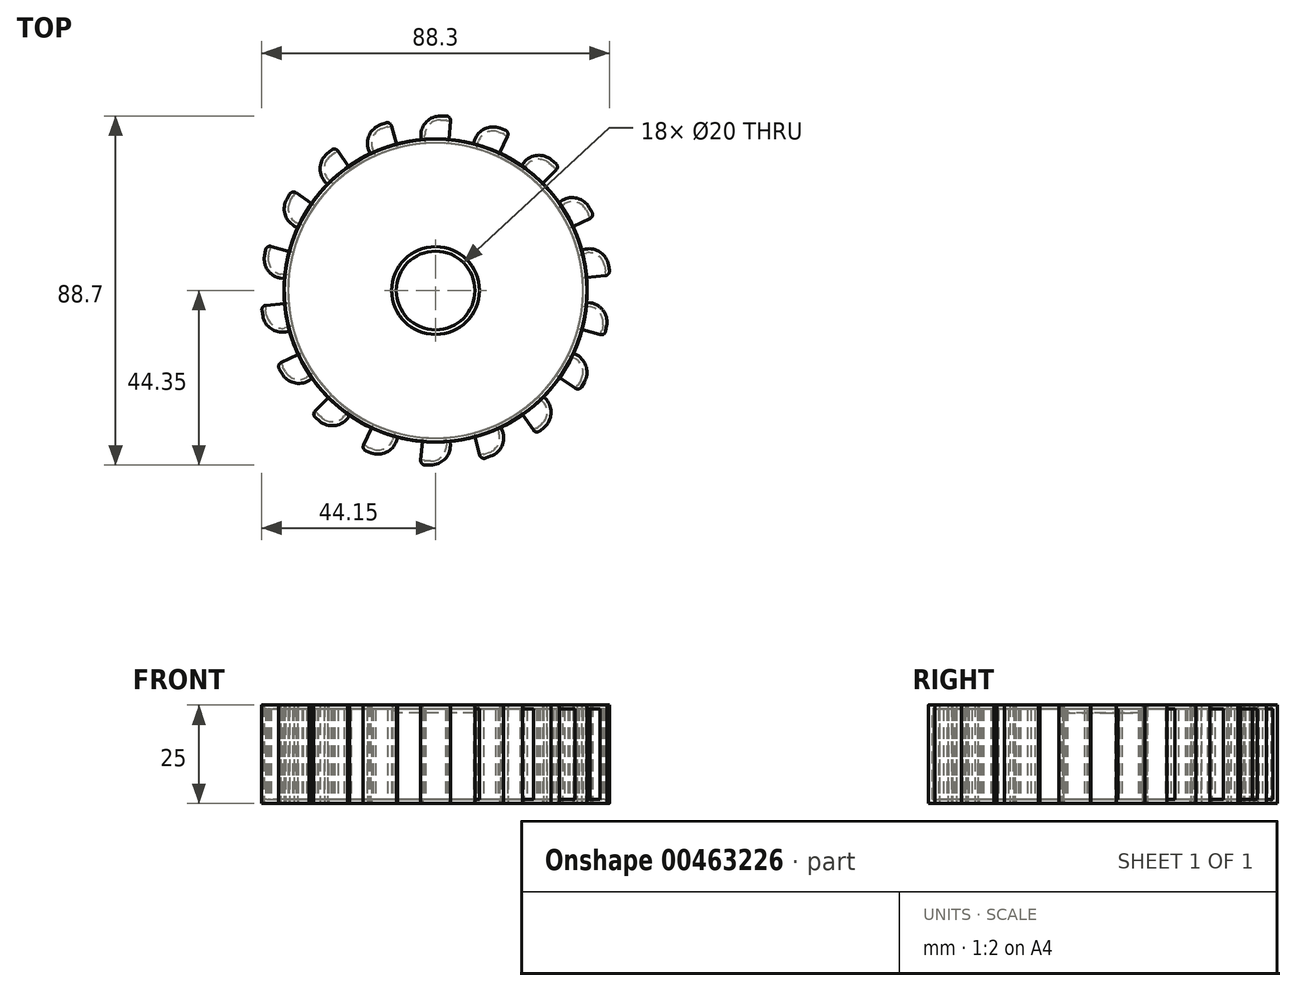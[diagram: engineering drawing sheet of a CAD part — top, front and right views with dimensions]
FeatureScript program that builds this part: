
annotation { "Feature Type Name" : "Feature", "Feature Type Description" : "" }
export const myFeature = defineFeature(function(context is Context, id is Id, definition is map)
    precondition{}
    {
        {
            var Q0;
            Q0=qCreatedBy(makeId("Top.planeOp"),FACE);
            var sketch = newSketch(context, id + "F0", { "sketchPlane" : qUnion([Q0])});
            skCircle(sketch, "E0", {"center": v(0, 0) * mm, "radius": 38.5 * mm});
            skLineSegment(sketch, "E1", {"start": v(1.24, 44.35) * mm, "end": v(2.65, 44.35) * mm});
            skArc(sketch, "E2.filletArc", {"start": v(1.24, 44.35) * mm, "mid": v(-2.3, 42.88) * mm, "end": v(-3.76, 39.35) * mm});
            skArc(sketch, "E3.filletArc", {"start": v(3.77, 43.12) * mm, "mid": v(3.48, 43.98) * mm, "end": v(2.65, 44.35) * mm});
            skLineSegment(sketch, "E4.trimOffspring", {"start": v(-3.67, 38.32) * mm, "end": v(-3.76, 39.35) * mm});
            skLineSegment(sketch, "E5.trimOffspring", {"start": v(3.35, 38.35) * mm, "end": v(3.77, 43.12) * mm});
            skPoint(sketch, "E6.orphan", {"position": v(0, 57.06) * mm});
            skCircle(sketch, "E7", {"center": v(0, 0) * mm, "radius": 10 * mm});
            skSolve(sketch);
        }
        {
            var Q0;
            {var subQ0=sQuery(id+"F0.wireOp",EDGE,"E0");var subQ1=makeQuery(id+"F0.imprint","INTERSECT",VERTEX,{"derivedFrom":[subQ0,sQuery(id+"F0.wireOp",EDGE,"E4.trimOffspring")]});Q0=makeQuery(id+"F0.imprint","IMPRINT",FACE,{"disambiguationData":[TD([[makeQuery(id+"F0.imprint","IMPRINT",EDGE,{"disambiguationData":[TD([[subQ1,1.0]])],"derivedFrom":subQ0}),1.0]])]});}
            var Q1;
            Q1=makeQuery(id+"F0.imprint","IMPRINT",FACE,{"disambiguationData":[TD([[makeQuery(id+"F0.imprint","IMPRINT",EDGE,{"derivedFrom":sQuery(id+"F0.wireOp",EDGE,"E1")}),-1.0]])]});
            extrude(context, id + "F1", {"entities" : qUnion([Q0, Q1]), "depth" : 25 * mm});
        }
        {
            var Q0;
            Q0=makeQuery(id+"F1.opExtrude","SWEPT_FACE",FACE,{"disambiguationData":[OSD([sQuery(id+"F0.wireOp",EDGE,"E5.trimOffspring")])]});
            shell(context, id + "F2", {"entities" : qUnion([Q0]), "thickness" : 1 * mm});
        }
        {
            var Q0;
            Q0=makeQuery(id+"F1.opExtrude","SWEPT_BODY",BODY,{"disambiguationData":[OSD([sQuery(id+"F0.wireOp",EDGE,"E0"),sQuery(id+"F0.wireOp",EDGE,"E1"),sQuery(id+"F0.wireOp",EDGE,"E2.filletArc"),sQuery(id+"F0.wireOp",EDGE,"E3.filletArc"),sQuery(id+"F0.wireOp",EDGE,"E4.trimOffspring"),sQuery(id+"F0.wireOp",EDGE,"E5.trimOffspring"),sQuery(id+"F0.wireOp",EDGE,"E7")])]});
            var Q1;
            Q1=makeQuery(id+"F1.opExtrude","SWEPT_FACE",FACE,{"disambiguationData":[OSD([sQuery(id+"F0.wireOp",EDGE,"E0")])]});
            circularPattern(context, id + "F3", {"entities" : qUnion([Q0]), "axis" : qUnion([Q1]), "angle" : 360 * degree, "instanceCount" : 18, "oppositeDirection" : true, "equalSpace" : true});
        }
        {
            var Q0;
            Q0=makeQuery(id+"F1.opExtrude","CAP_EDGE",EDGE,{"disambiguationData":[OSD([sQuery(id+"F0.wireOp",EDGE,"E7")])],"isStart":false});
            chamfer(context, id + "F4", {"entities" : qUnion([Q0]), "chamferType" : ChamferType.OFFSET_ANGLE, "width" : 2 * mm, "oppositeDirection" : false, "angle" : 30 * degree, "tangentPropagation" : true});
        }
    });
